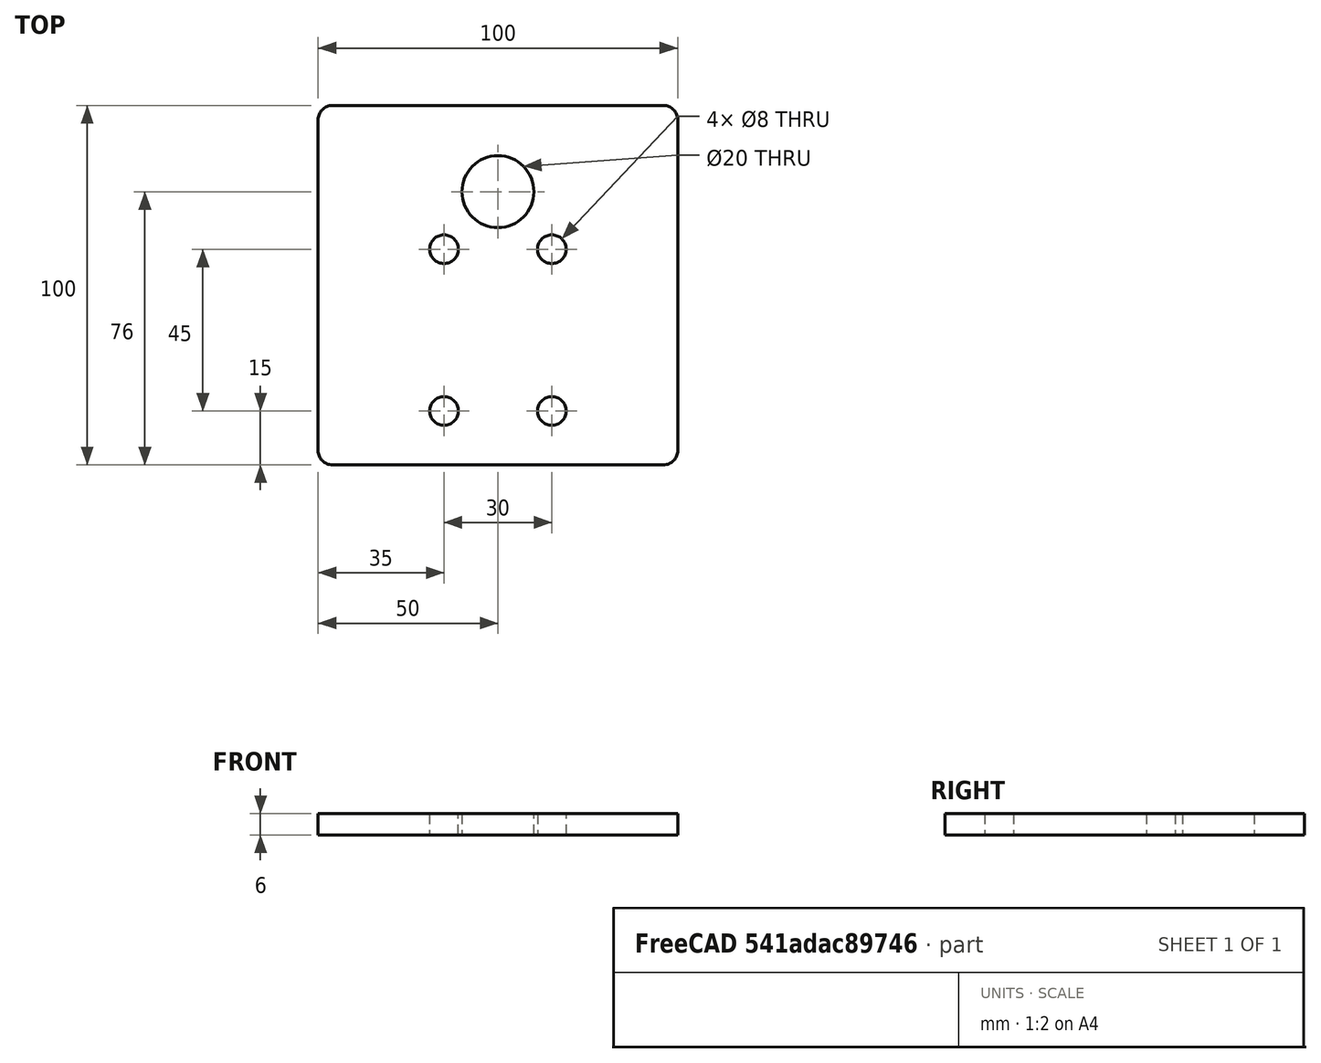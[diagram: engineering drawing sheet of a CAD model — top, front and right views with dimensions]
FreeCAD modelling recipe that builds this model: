
FCSTD DOCUMENT  (FreeCAD 0.15R4671 (Git))
Label: Plaque support
License: All rights reserved
LicenseURL: http://fr.wikipedia.org/wiki/<copyright redacted>
objects: Sketcher::SketchObject×1, PartDesign::Pad×1
note: 3 computed .brp shape members not serialized (recipe doc carries the construction recipe); baked Part::Feature solids carry a one-line shape summary decoded from their .brp

FEATURE [Sketcher::SketchObject] Sketch
  sketch-geometry (23):
    g0: LineSegment StartX=-46 StartY=50 StartZ=0 EndX=46 EndY=50 EndZ=0
    g1: LineSegment StartX=50 StartY=46 StartZ=0 EndX=50 EndY=-46 EndZ=0
    g2: LineSegment StartX=46 StartY=-50 StartZ=0 EndX=-46 EndY=-50 EndZ=0
    g3: LineSegment StartX=-50 StartY=-46 StartZ=0 EndX=-50 EndY=46 EndZ=0
    g4: LineSegment [constr] StartX=-46 StartY=46 StartZ=0 EndX=0 EndY=0 EndZ=0
    g5: LineSegment [constr] StartX=0 StartY=0 StartZ=0 EndX=46 EndY=46 EndZ=0
    g6: LineSegment [constr] StartX=-46 StartY=-46 StartZ=0 EndX=0 EndY=0 EndZ=0
    g7: LineSegment [constr] StartX=0 StartY=0 StartZ=0 EndX=46 EndY=-46 EndZ=0
    g8: Circle CenterX=0 CenterY=26 CenterZ=0 NormalX=0 NormalY=0 NormalZ=1 Radius=10
    g9: Circle CenterX=-15 CenterY=-35 CenterZ=0 NormalX=0 NormalY=0 NormalZ=1 Radius=4
    g10: Circle CenterX=-15 CenterY=10 CenterZ=0 NormalX=0 NormalY=0 NormalZ=1 Radius=4
    g11: Circle CenterX=15 CenterY=10 CenterZ=0 NormalX=0 NormalY=0 NormalZ=1 Radius=4
    g12: Circle CenterX=15 CenterY=-35 CenterZ=0 NormalX=0 NormalY=0 NormalZ=1 Radius=4
    g13: LineSegment [constr] StartX=-15 StartY=10 StartZ=0 EndX=15 EndY=10 EndZ=0
    g14: LineSegment [constr] StartX=15 StartY=10 StartZ=0 EndX=15 EndY=-35 EndZ=0
    g15: LineSegment [constr] StartX=15 StartY=-35 StartZ=0 EndX=-15 EndY=-35 EndZ=0
    g16: LineSegment [constr] StartX=-15 StartY=-35 StartZ=0 EndX=-15 EndY=10 EndZ=0
    g17: LineSegment [constr] StartX=-15 StartY=-35 StartZ=0 EndX=-46 EndY=-46 EndZ=0
    g18: LineSegment [constr] StartX=15 StartY=-35 StartZ=0 EndX=46 EndY=-46 EndZ=0
    g19: ArcOfCircle CenterX=-46 CenterY=46 CenterZ=0 NormalX=0 NormalY=0 NormalZ=1 Radius=4 StartAngle=1.5708 EndAngle=3.14159
    g20: ArcOfCircle CenterX=46 CenterY=46 CenterZ=0 NormalX=0 NormalY=0 NormalZ=1 Radius=4 StartAngle=0 EndAngle=1.5708
    g21: ArcOfCircle CenterX=46 CenterY=-46 CenterZ=0 NormalX=0 NormalY=0 NormalZ=1 Radius=4 StartAngle=4.71239 EndAngle=6.28319
    g22: ArcOfCircle CenterX=-46 CenterY=-46 CenterZ=0 NormalX=0 NormalY=0 NormalZ=1 Radius=4 StartAngle=3.14159 EndAngle=4.71239
  constraints (55):
    c: Horizontal(g0)
    c: Horizontal(g2)
    c: Vertical(g1)
    c: Vertical(g3)
    c: Coincident(g4,g-1)
    c: Coincident(g4,g5)
    c: Coincident(g6,g-1)
    c: Coincident(g6,g7)
    c: Equal(g7,g6)
    c: Equal(g6,g4)
    c: Equal(g4,g5)
    c: PointOnObject(g8,g-2)
    c: Coincident(g13,g10)
    c: Coincident(g13,g11)
    c: Horizontal(g13)
    c: Coincident(g13,g14)
    c: Coincident(g14,g12)
    c: Coincident(g14,g15)
    c: Coincident(g15,g9)
    c: Horizontal(g15)
    c: Coincident(g15,g16)
    c: Coincident(g16,g13)
    c: Vertical(g16)
    c: Vertical(g14)
    c: Equal(g11,g12)
    c: Equal(g12,g9)
    c: Equal(g9,g10)
    c: Coincident(g17,g9)
    c: Coincident(g17,g6)
    c: Coincident(g18,g12)
    c: Coincident(g18,g7)
    c: Equal(g17,g18)
    c: Radius(g10) = 4
    c: Radius(g8) = 10
    c: DistanceY(g8,g5) = 20
    c: Tangent(g0,g19) = 1.5708
    c: Tangent(g3,g19) = 1.5708
    c: Tangent(g0,g20) = 1.5708
    c: Tangent(g1,g20) = 1.5708
    c: Tangent(g2,g21) = 1.5708
    c: Tangent(g1,g21) = 1.5708
    c: Tangent(g2,g22) = 1.5708
    c: Tangent(g3,g22) = 1.5708
    c: Coincident(g19,g4)
    c: Coincident(g20,g5)
    c: Coincident(g21,g7)
    c: Coincident(g22,g6)
    c: Equal(g19,g20)
    c: Equal(g20,g21)
    c: Radius(g19) = 4
    c: DistanceY(g9,g2) = -15
    c: DistanceY(g12,g11) = 45
    c: DistanceY(g0,g2) = -100
    c: DistanceX(g3,g1) = 100
    c: DistanceX(g9,g12) = 30
FEATURE [PartDesign::Pad] Pad
  Length = 6
  Length2 = 100
  Sketch = -> Sketch
  Type = 0
